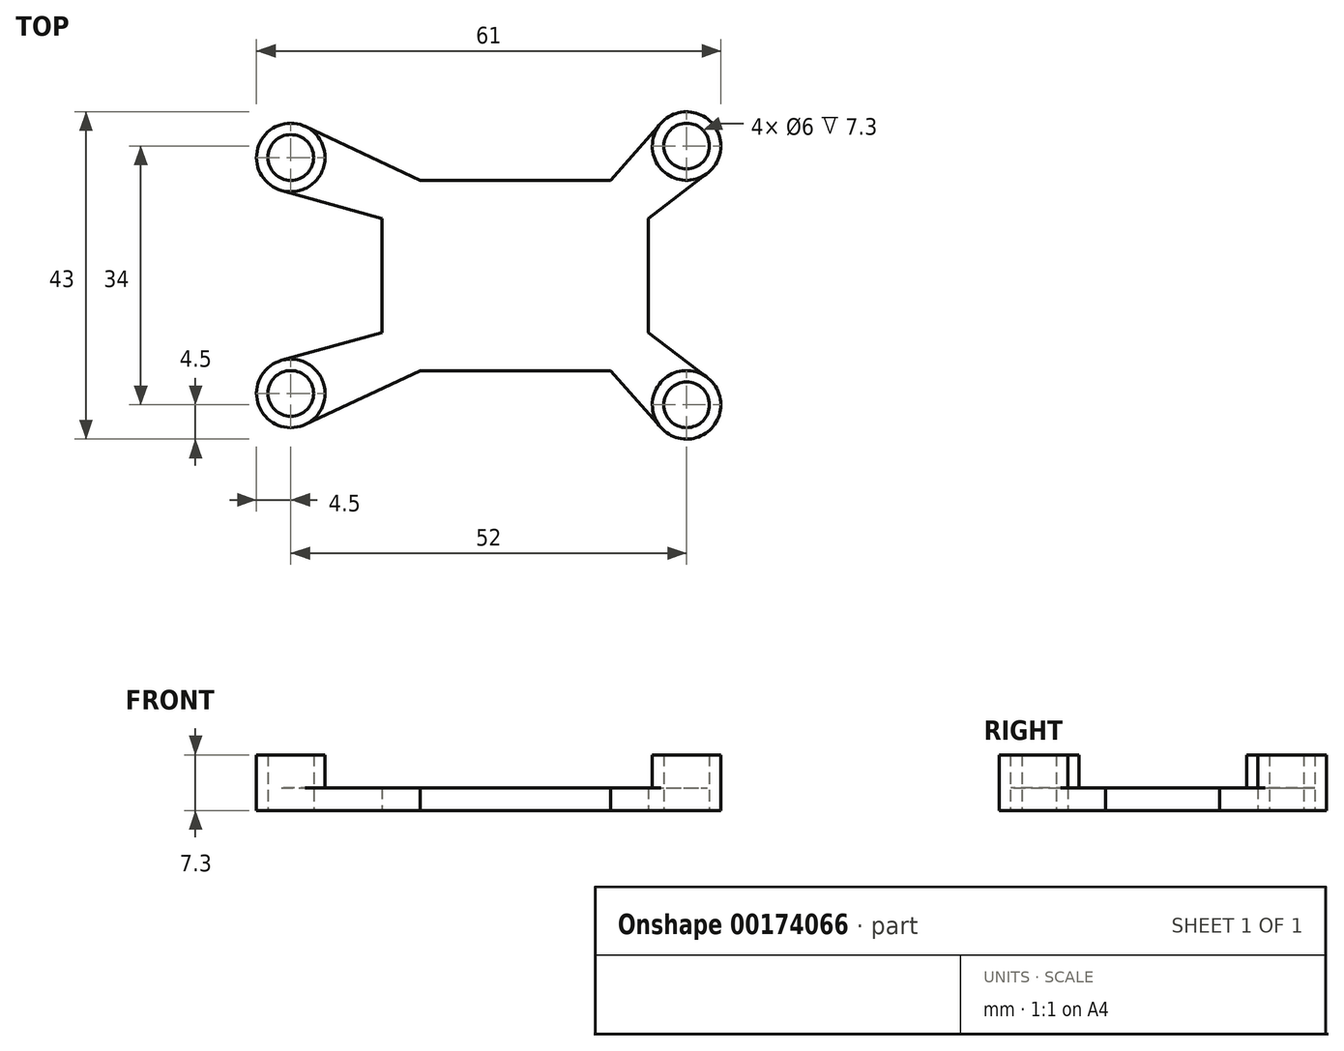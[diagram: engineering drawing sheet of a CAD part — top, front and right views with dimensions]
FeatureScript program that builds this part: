
annotation { "Feature Type Name" : "Feature", "Feature Type Description" : "" }
export const myFeature = defineFeature(function(context is Context, id is Id, definition is map)
    precondition{}
    {
        {
            var Q0;
            Q0=qCreatedBy(makeId("Top.planeOp"),FACE);
            var sketch = newSketch(context, id + "F0", { "sketchPlane" : qUnion([Q0])});
            skCircle(sketch, "E0", {"center": v(-52, 15.5) * mm, "radius": 4.5 * mm});
            skCircle(sketch, "E1", {"center": v(-52, -15.5) * mm, "radius": 4.5 * mm});
            skCircle(sketch, "E2", {"center": v(0, 17) * mm, "radius": 4.5 * mm});
            skCircle(sketch, "E3", {"center": v(0, -17) * mm, "radius": 4.5 * mm});
            skLineSegment(sketch, "E4.bottom", {"start": v(-40, 12.5) * mm, "end": v(-5, 12.5) * mm});
            skLineSegment(sketch, "E4.top", {"start": v(-40, -12.5) * mm, "end": v(-5, -12.5) * mm});
            skLineSegment(sketch, "E4.left", {"start": v(-40, 12.5) * mm, "end": v(-40, -12.5) * mm});
            skLineSegment(sketch, "E4.right", {"start": v(-5, 12.5) * mm, "end": v(-5, -12.5) * mm});
            skCircle(sketch, "E5", {"center": v(-52, 15.5) * mm, "radius": 3 * mm});
            skCircle(sketch, "E6", {"center": v(-52, -15.5) * mm, "radius": 3 * mm});
            skCircle(sketch, "E7", {"center": v(0, 17) * mm, "radius": 3 * mm});
            skCircle(sketch, "E8", {"center": v(0, -17) * mm, "radius": 3 * mm});
            skLineSegment(sketch, "E9", {"start": v(-35, 12.5) * mm, "end": v(-50.09, 19.57) * mm});
            skLineSegment(sketch, "E10", {"start": v(-40, 7.5) * mm, "end": v(-53.2, 11.16) * mm});
            skLineSegment(sketch, "E11", {"start": v(-40, -7.5) * mm, "end": v(-53.2, -11.16) * mm});
            skLineSegment(sketch, "E12", {"start": v(-35, -12.5) * mm, "end": v(-50.09, -19.57) * mm});
            skLineSegment(sketch, "E13", {"start": v(-10, -12.5) * mm, "end": v(-3.37, -19.98) * mm});
            skLineSegment(sketch, "E14", {"start": v(-5, -7.5) * mm, "end": v(2.74, -13.43) * mm});
            skLineSegment(sketch, "E15", {"start": v(-5, 7.5) * mm, "end": v(2.74, 13.43) * mm});
            skLineSegment(sketch, "E16", {"start": v(-10, 12.5) * mm, "end": v(-3.37, 19.98) * mm});
            skSolve(sketch);
        }
        {
            var Q0;
            {var subQ0=sQuery(id+"F0.wireOp",EDGE,"E4.left");var subQ3=sQuery(id+"F0.wireOp",EDGE,"E4.bottom");var subQ4=makeQuery(id+"F0.imprint","INTERSECT",VERTEX,{"derivedFrom":[subQ3,subQ0]});Q0=makeQuery(id+"F0.imprint","IMPRINT",FACE,{"disambiguationData":[TD([[makeQuery(id+"F0.imprint","IMPRINT",EDGE,{"disambiguationData":[TD([[subQ4,-1.0]])],"derivedFrom":subQ3}),-1.0]])]});}
            var Q1;
            {var subQ0=sQuery(id+"F0.wireOp",EDGE,"E15");Q1=makeQuery(id+"F0.imprint","IMPRINT",FACE,{"disambiguationData":[TD([[makeQuery(id+"F0.imprint","IMPRINT",EDGE,{"derivedFrom":subQ0}),1.0]])]});}
            var Q2;
            {var subQ4=sQuery(id+"F0.wireOp",EDGE,"E9");Q2=makeQuery(id+"F0.imprint","IMPRINT",FACE,{"disambiguationData":[TD([[makeQuery(id+"F0.imprint","IMPRINT",EDGE,{"derivedFrom":subQ4}),1.0]])]});}
            var Q3;
            {var subQ0=sQuery(id+"F0.wireOp",EDGE,"E11");Q3=makeQuery(id+"F0.imprint","IMPRINT",FACE,{"disambiguationData":[TD([[makeQuery(id+"F0.imprint","IMPRINT",EDGE,{"derivedFrom":subQ0}),1.0]])]});}
            var Q4;
            {var subQ0=sQuery(id+"F0.wireOp",EDGE,"E13");Q4=makeQuery(id+"F0.imprint","IMPRINT",FACE,{"disambiguationData":[TD([[makeQuery(id+"F0.imprint","IMPRINT",EDGE,{"derivedFrom":subQ0}),1.0]])]});}
            extrude(context, id + "F1", {"entities" : qUnion([Q0, Q1, Q2, Q3, Q4]), "depth" : 3 * mm});
        }
        {
            var Q0;
            Q0=makeQuery(id+"F0.imprint","IMPRINT",FACE,{"disambiguationData":[TD([[makeQuery(id+"F0.imprint","IMPRINT",EDGE,{"derivedFrom":sQuery(id+"F0.wireOp",EDGE,"E6")}),-1.0]])]});
            var Q1;
            Q1=makeQuery(id+"F0.imprint","IMPRINT",FACE,{"disambiguationData":[TD([[makeQuery(id+"F0.imprint","IMPRINT",EDGE,{"derivedFrom":sQuery(id+"F0.wireOp",EDGE,"E5")}),-1.0]])]});
            var Q2;
            Q2=makeQuery(id+"F0.imprint","IMPRINT",FACE,{"disambiguationData":[TD([[makeQuery(id+"F0.imprint","IMPRINT",EDGE,{"derivedFrom":sQuery(id+"F0.wireOp",EDGE,"E8")}),-1.0]])]});
            var Q3;
            Q3=makeQuery(id+"F0.imprint","IMPRINT",FACE,{"disambiguationData":[TD([[makeQuery(id+"F0.imprint","IMPRINT",EDGE,{"derivedFrom":sQuery(id+"F0.wireOp",EDGE,"E7")}),-1.0]])]});
            extrude(context, id + "F2", {"entities" : qUnion([Q0, Q1, Q2, Q3]), "operationType" : NewBodyOperationType.ADD, "depth" : 7.3 * mm});
        }
    });
